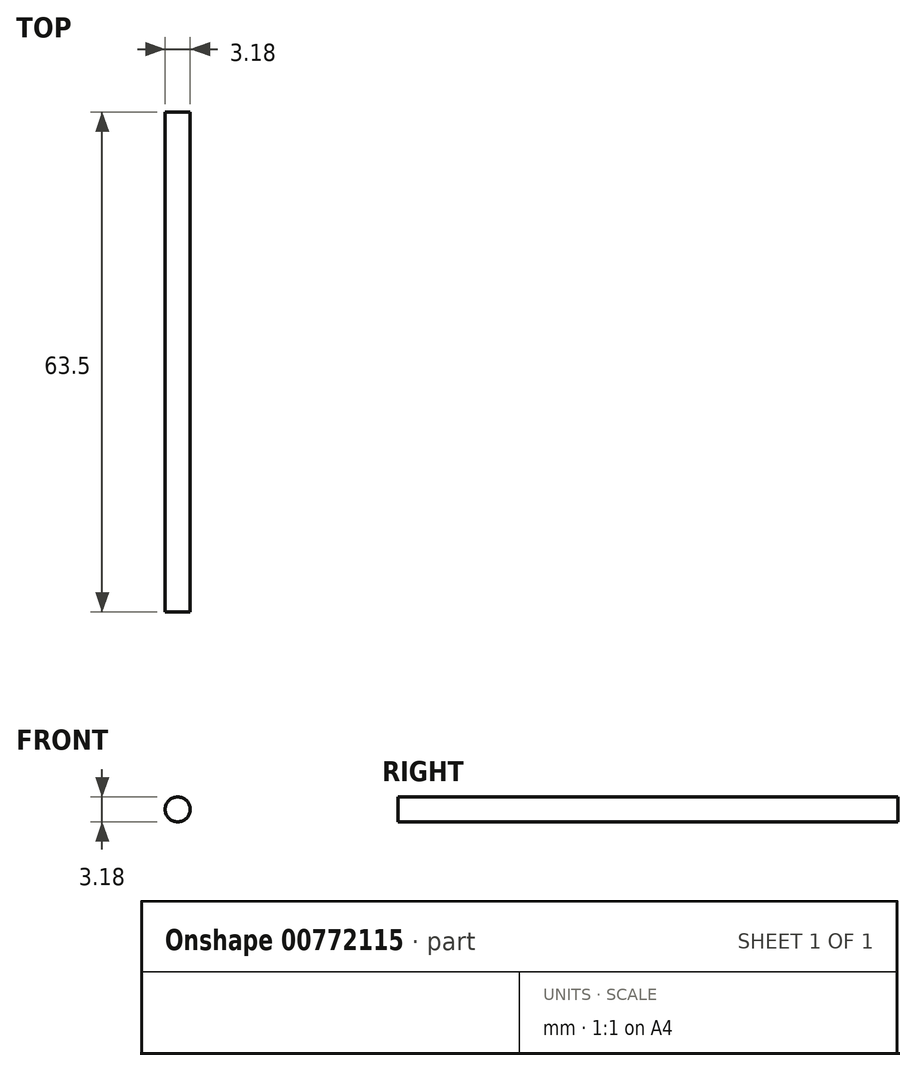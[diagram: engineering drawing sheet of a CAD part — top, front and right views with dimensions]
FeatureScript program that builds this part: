
annotation { "Feature Type Name" : "Feature", "Feature Type Description" : "" }
export const myFeature = defineFeature(function(context is Context, id is Id, definition is map)
    precondition{}
    {
        {
            var Q0;
            Q0=qCreatedBy(makeId("Front.planeOp"),FACE);
            var sketch = newSketch(context, id + "F0", { "sketchPlane" : qUnion([Q0])});
            skCircle(sketch, "E0", {"center": v(0, 0) * mm, "radius": 1.59 * mm});
            skSolve(sketch);
        }
        {
            var Q0;
            Q0=qSketchRegion(id+"F0",true);
            extrude(context, id + "F1", {"entities" : qUnion([Q0]), "depth" : 63.5 * mm, "offsetDistance" : 25.4 * mm});
        }
    });
